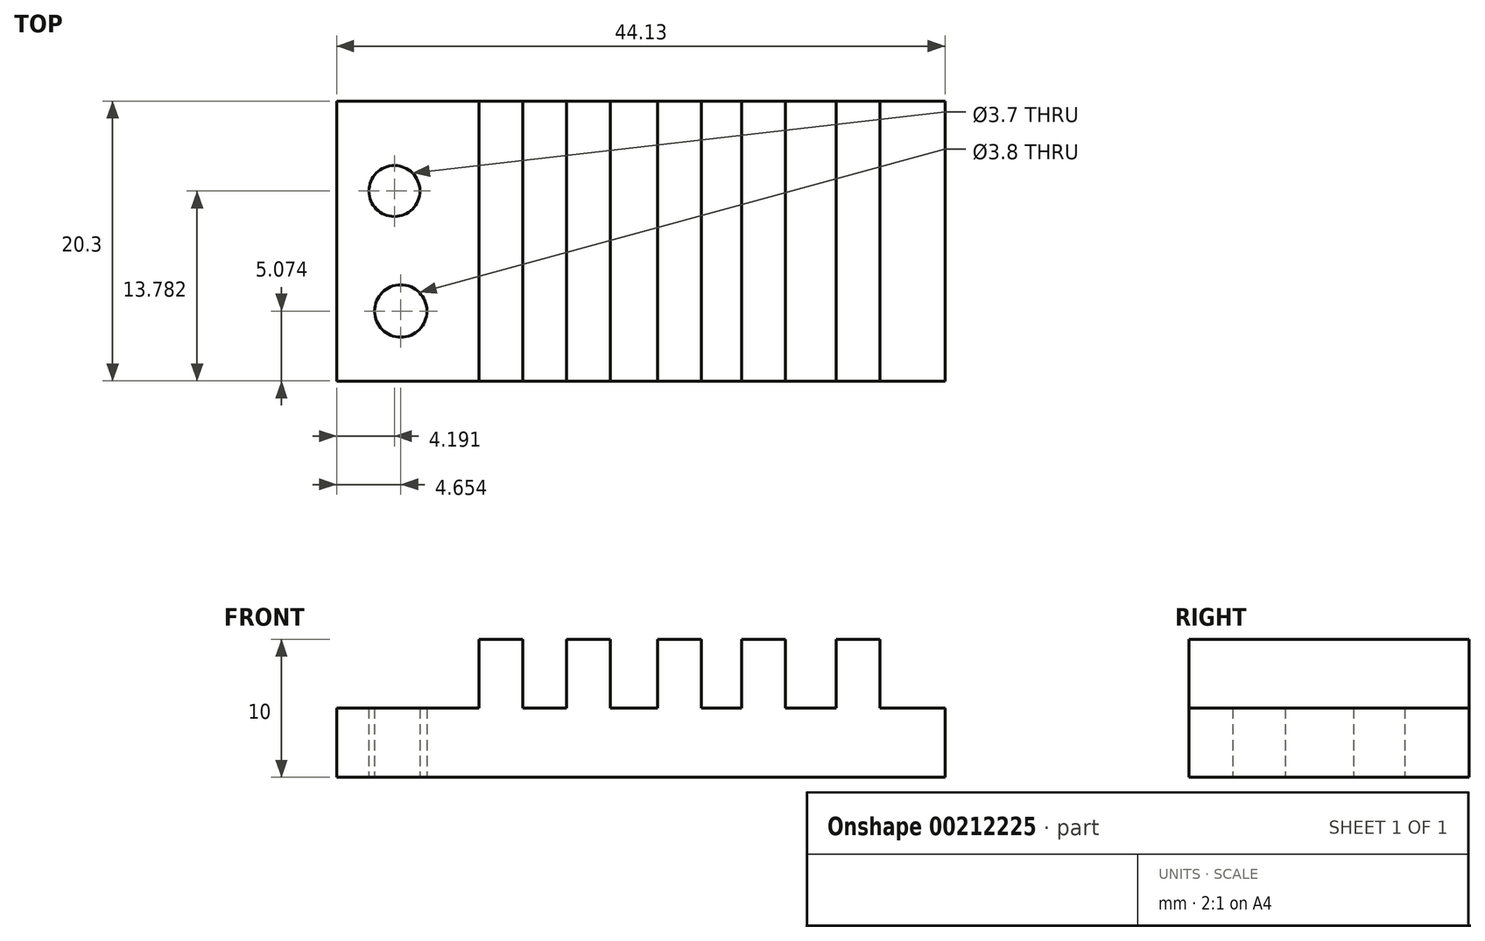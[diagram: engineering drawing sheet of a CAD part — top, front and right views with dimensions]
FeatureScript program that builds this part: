
annotation { "Feature Type Name" : "Feature", "Feature Type Description" : "" }
export const myFeature = defineFeature(function(context is Context, id is Id, definition is map)
    precondition{}
    {
        {
            var Q0;
            Q0=qCreatedBy(makeId("Top.planeOp"),FACE);
            var sketch = newSketch(context, id + "F0", { "sketchPlane" : qUnion([Q0])});
            skLineSegment(sketch, "E0.bottom", {"start": v(-44.9, -50.75) * mm, "end": v(-0.78, -50.75) * mm});
            skLineSegment(sketch, "E0.top", {"start": v(-44.9, -30.45) * mm, "end": v(-0.78, -30.45) * mm});
            skLineSegment(sketch, "E0.left", {"start": v(-44.9, -50.75) * mm, "end": v(-44.9, -30.45) * mm});
            skLineSegment(sketch, "E0.right", {"start": v(-0.78, -50.75) * mm, "end": v(-0.78, -30.45) * mm});
            skPoint(sketch, "E1.endSnap0", {"position": v(4.98, -50.77) * mm});
            skSolve(sketch);
        }
        {
            var Q0;
            Q0=qSketchRegion(id+"F0",true);
            extrude(context, id + "F1", {"entities" : qUnion([Q0]), "oppositeDirection" : true, "depth" : 5 * mm});
        }
        {
            var Q0;
            Q0=makeQuery(id+"F1.opExtrude","CAP_FACE",FACE,{"disambiguationData":[OSD([sQuery(id+"F0.wireOp",EDGE,"E0.bottom"),sQuery(id+"F0.wireOp",EDGE,"E0.top"),sQuery(id+"F0.wireOp",EDGE,"E0.left"),sQuery(id+"F0.wireOp",EDGE,"E0.right")])],"isStart":true});
            var sketch = newSketch(context, id + "F2", { "sketchPlane" : qUnion([Q0])});
            skLineSegment(sketch, "E2.bottom", {"start": v(-34.58, -30.45) * mm, "end": v(-31.4, -30.45) * mm});
            skLineSegment(sketch, "E2.top", {"start": v(-34.58, -50.75) * mm, "end": v(-31.4, -50.75) * mm});
            skLineSegment(sketch, "E2.left", {"start": v(-34.58, -30.45) * mm, "end": v(-34.58, -50.75) * mm});
            skLineSegment(sketch, "E2.right", {"start": v(-31.4, -30.45) * mm, "end": v(-31.4, -50.75) * mm});
            skLineSegment(sketch, "E3", {"start": v(-31.4, -30.45) * mm, "end": v(-28.23, -30.45) * mm});
            skLineSegment(sketch, "E4.1.0.0", {"start": v(-25.06, -30.45) * mm, "end": v(-25.06, -50.75) * mm});
            skLineSegment(sketch, "E4.1.0.1", {"start": v(-28.23, -30.45) * mm, "end": v(-25.06, -30.45) * mm});
            skLineSegment(sketch, "E4.1.0.2", {"start": v(-28.23, -30.45) * mm, "end": v(-28.23, -50.75) * mm});
            skLineSegment(sketch, "E4.1.0.3", {"start": v(-28.23, -50.75) * mm, "end": v(-25.06, -50.75) * mm});
            skLineSegment(sketch, "E4.direction1", {"start": v(-31.4, -50.75) * mm, "end": v(-25.06, -50.75) * mm, "construction": true});
            skLineSegment(sketch, "E5", {"start": v(-25.06, -30.45) * mm, "end": v(-21.63, -30.45) * mm});
            skLineSegment(sketch, "E6.bottom", {"start": v(-21.63, -30.45) * mm, "end": v(-18.45, -30.45) * mm});
            skLineSegment(sketch, "E6.top", {"start": v(-21.63, -50.75) * mm, "end": v(-18.45, -50.75) * mm});
            skLineSegment(sketch, "E6.left", {"start": v(-21.63, -30.45) * mm, "end": v(-21.63, -50.75) * mm});
            skLineSegment(sketch, "E6.right", {"start": v(-18.45, -30.45) * mm, "end": v(-18.45, -50.75) * mm});
            skLineSegment(sketch, "E7", {"start": v(-18.45, -30.45) * mm, "end": v(-15.53, -30.45) * mm});
            skLineSegment(sketch, "E8.bottom", {"start": v(-15.53, -30.45) * mm, "end": v(-12.36, -30.45) * mm});
            skLineSegment(sketch, "E8.top", {"start": v(-15.53, -50.75) * mm, "end": v(-12.36, -50.75) * mm});
            skLineSegment(sketch, "E8.left", {"start": v(-15.53, -30.45) * mm, "end": v(-15.53, -50.75) * mm});
            skLineSegment(sketch, "E8.right", {"start": v(-12.36, -30.45) * mm, "end": v(-12.36, -50.75) * mm});
            skLineSegment(sketch, "E9", {"start": v(-12.36, -30.45) * mm, "end": v(-8.67, -30.45) * mm});
            skLineSegment(sketch, "E10.bottom", {"start": v(-8.67, -30.45) * mm, "end": v(-5.5, -30.45) * mm});
            skLineSegment(sketch, "E10.top", {"start": v(-8.67, -50.75) * mm, "end": v(-5.5, -50.75) * mm});
            skLineSegment(sketch, "E10.left", {"start": v(-8.67, -30.45) * mm, "end": v(-8.67, -50.75) * mm});
            skLineSegment(sketch, "E10.right", {"start": v(-5.5, -30.45) * mm, "end": v(-5.5, -50.75) * mm});
            skSolve(sketch);
        }
        {
            var Q0;
            Q0=qSketchRegion(id+"F2",true);
            extrude(context, id + "F3", {"entities" : qUnion([Q0]), "operationType" : NewBodyOperationType.ADD, "depth" : 5 * mm});
        }
        {
            var Q0;
            Q0=makeQuery(id+"F1.boolean.opBoolean","MERGE",FACE,{"derivedFrom":[makeQuery(id+"FrM0S1BdwquSU4h_1.opExtrude","CAP_FACE",FACE,{"disambiguationData":[OSD([sQuery(id+"F1paRBLzH6P92U9_1.wireOp",EDGE,"ca1a8222-2888-463a-b1ca-637cd0208124.0"),sQuery(id+"F1paRBLzH6P92U9_1.wireOp",EDGE,"ca1a8222-2888-463a-b1ca-637cd0208124.1"),sQuery(id+"F1paRBLzH6P92U9_1.wireOp",EDGE,"ca1a8222-2888-463a-b1ca-637cd0208124.2"),sQuery(id+"F1paRBLzH6P92U9_1.wireOp",EDGE,"ca1a8222-2888-463a-b1ca-637cd0208124.3")])],"isStart":true}),makeQuery(id+"F1.opExtrude","CAP_FACE",FACE,{"disambiguationData":[OSD([sQuery(id+"F0.wireOp",EDGE,"E0.bottom"),sQuery(id+"F0.wireOp",EDGE,"E0.top"),sQuery(id+"F0.wireOp",EDGE,"E0.left"),sQuery(id+"F0.wireOp",EDGE,"E0.right")])],"isStart":false})]});
            var sketch = newSketch(context, id + "F4", { "sketchPlane" : qUnion([Q0])});
            skCircle(sketch, "E11", {"center": v(-40.26, 45.68) * mm, "radius": 1.9 * mm});
            skLineSegment(sketch, "E12", {"start": v(-44.9, 50.75) * mm, "end": v(-41.4, 50.75) * mm});
            skCircle(sketch, "E13", {"center": v(-40.72, 36.97) * mm, "radius": 1.85 * mm});
            skSolve(sketch);
        }
        {
            var Q0;
            Q0=qSketchRegion(id+"F4",true);
            extrude(context, id + "F5", {"entities" : qUnion([Q0]), "operationType" : NewBodyOperationType.REMOVE, "endBound" : BoundingType.THROUGH_ALL, "oppositeDirection" : true, "depth" : 25.4 * mm});
        }
    });
